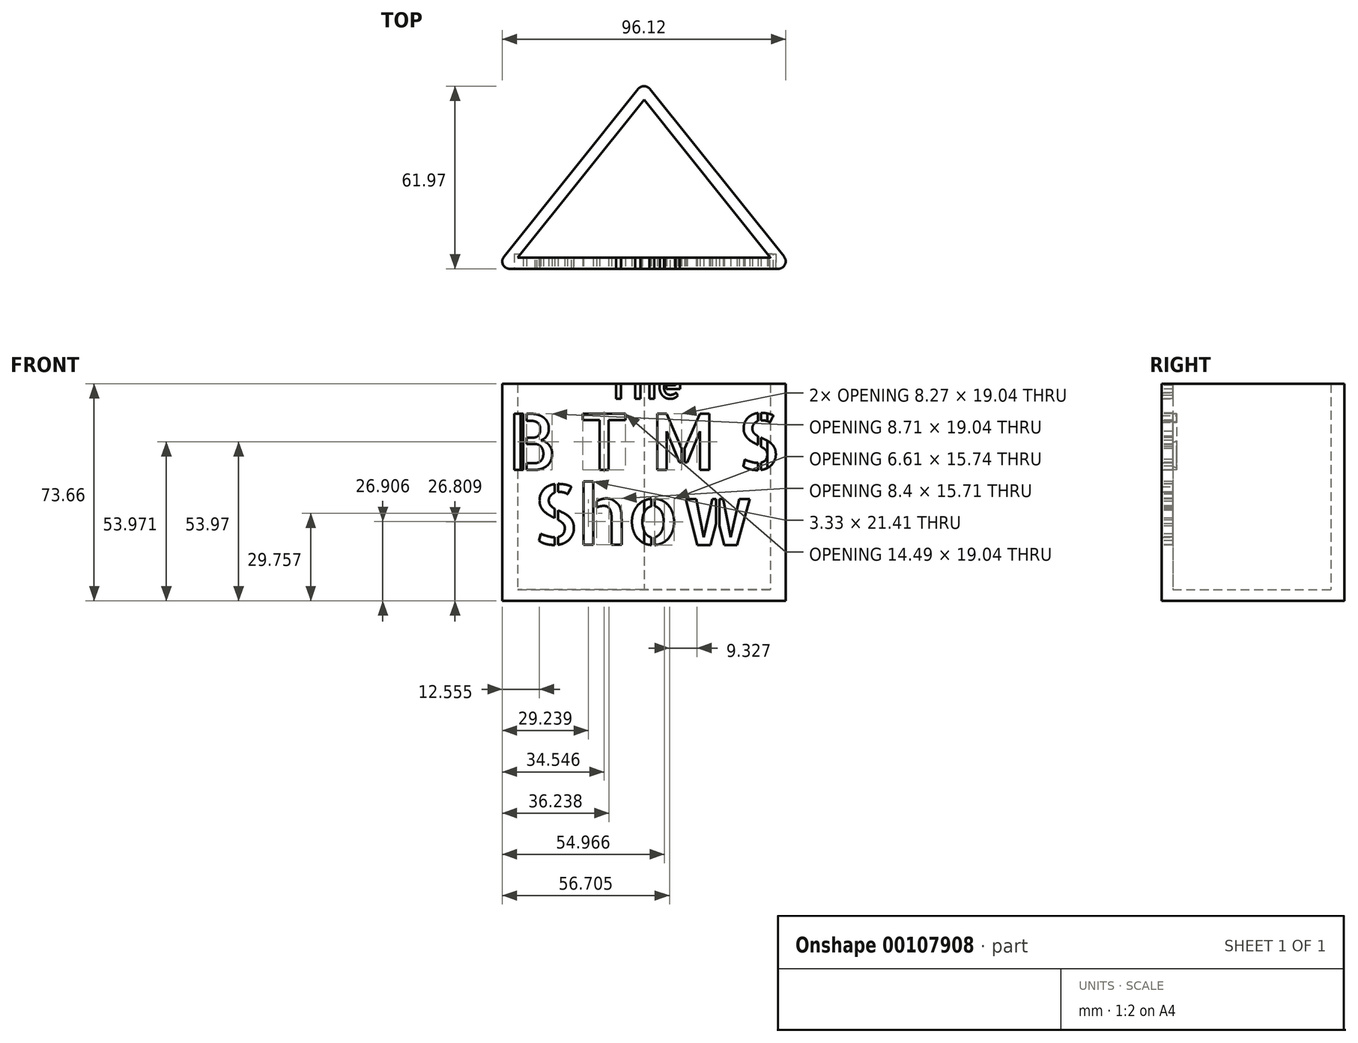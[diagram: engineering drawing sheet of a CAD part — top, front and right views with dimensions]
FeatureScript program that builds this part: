
annotation { "Feature Type Name" : "Feature", "Feature Type Description" : "" }
export const myFeature = defineFeature(function(context is Context, id is Id, definition is map)
    precondition{}
    {
        {
            var Q0;
            Q0=qCreatedBy(makeId("Top.planeOp"),FACE);
            var sketch = newSketch(context, id + "F0", { "sketchPlane" : qUnion([Q0])});
            skLineSegment(sketch, "E0", {"start": v(0, 0) * mm, "end": v(50.8, -63.5) * mm});
            skLineSegment(sketch, "E1", {"start": v(50.8, -63.5) * mm, "end": v(-50.8, -63.5) * mm});
            skLineSegment(sketch, "E2", {"start": v(-50.8, -63.5) * mm, "end": v(0, 0) * mm});
            skLineSegment(sketch, "E3", {"start": v(0, 0) * mm, "end": v(0, -63.5) * mm, "construction": true});
            skSolve(sketch);
        }
        {
            var Q0;
            Q0=makeQuery(id+"F0.imprint","IMPRINT",FACE,{"disambiguationData":[TD([[makeQuery(id+"F0.imprint","IMPRINT",EDGE,{"derivedFrom":sQuery(id+"F0.wireOp",EDGE,"E0")}),-1.0]])]});
            extrude(context, id + "F1", {"entities" : qUnion([Q0]), "depth" : 3.8 * mm});
        }
        {
            var Q0;
            Q0=makeQuery(id+"F1.opExtrude","CAP_FACE",FACE,{"disambiguationData":[OSD([sQuery(id+"F0.wireOp",EDGE,"E0"),sQuery(id+"F0.wireOp",EDGE,"E1"),sQuery(id+"F0.wireOp",EDGE,"E2")])],"isStart":false});
            var sketch = newSketch(context, id + "F2", { "sketchPlane" : qUnion([Q0])});
            skLineSegment(sketch, "E4.0", {"start": v(42.87, -59.7) * mm, "end": v(0, -6.1) * mm});
            skLineSegment(sketch, "E4.1", {"start": v(-42.87, -59.7) * mm, "end": v(42.87, -59.69) * mm});
            skLineSegment(sketch, "E4.2", {"start": v(0, -6.1) * mm, "end": v(-42.87, -59.7) * mm});
            skSolve(sketch);
        }
        {
            var Q0;
            Q0=makeQuery(id+"F2.imprint","IMPRINT",FACE,{"disambiguationData":[TD([[makeQuery(id+"F2.imprint","IMPRINT",EDGE,{"derivedFrom":sQuery(id+"F2.wireOp",EDGE,"E4.0")}),-1.0]])]});
            extrude(context, id + "F3", {"entities" : qUnion([Q0]), "operationType" : NewBodyOperationType.ADD, "depth" : 69.85 * mm});
        }
        {
            var Q0;
            {var subQ0=sQuery(id+"F0.wireOp",EDGE,"E1");Q0=makeQuery(id+"F3.boolean.opBoolean","MERGE",FACE,{"derivedFrom":[makeQuery(id+"F1.opExtrude","SWEPT_FACE",FACE,{"disambiguationData":[OSD([subQ0])]}),makeQuery(id+"F3.opExtrude","SWEPT_FACE",FACE,{"disambiguationData":[OSD([subQ0])]})]});}
            var sketch = newSketch(context, id + "F4", { "sketchPlane" : qUnion([Q0])});
            skText(sketch, "E5", { "text": "The", "fontName": "AllertaStencil-Regular.ttf"});
            skText(sketch, "E6", { "text": "B T M S", "fontName": "AllertaStencil-Regular.ttf"});
            skText(sketch, "E7", { "text": "Show", "fontName": "AllertaStencil-Regular.ttf"});
            skLineSegment(sketch, "E8", {"start": v(0, 73.66) * mm, "end": v(0, 0) * mm, "construction": true});
            const initialGuessF4  = {"E5": [-0.01326, 0.06858, 1, 0, 0.01016], "E6": [-0.0465, 0.04445, 1, 0, 0.01905], "E7": [-0.0378, 0.01905, 1, 0, 0.02032]};
            skSetInitialGuess(sketch, initialGuessF4);
            skSolve(sketch);
        }
        {
            var Q0;
            Q0 = qSketchRegion(id + "F4", true);
            extrude(context, id + "F5", {"entities" : qUnion([Q0]), "operationType" : NewBodyOperationType.REMOVE, "oppositeDirection" : true, "depth" : 5.08 * mm});
        }
        {
            var Q0;
            {var subQ0=sQuery(id+"F0.wireOp",EDGE,"E2");var subQ1=sQuery(id+"F0.wireOp",EDGE,"E0");Q0=makeQuery(id+"F3.boolean.opBoolean","MERGE",EDGE,{"derivedFrom":[makeQuery(id+"F1.opExtrude","SWEPT_EDGE",EDGE,{"disambiguationData":[OSD([subQ1,subQ0])]}),makeQuery(id+"F3.opExtrude","SWEPT_EDGE",EDGE,{"disambiguationData":[OSD([subQ1,subQ0])]})]});}
            var Q1;
            {var subQ0=sQuery(id+"F0.wireOp",EDGE,"E1");var subQ1=sQuery(id+"F0.wireOp",EDGE,"E0");Q1=makeQuery(id+"F3.boolean.opBoolean","MERGE",EDGE,{"derivedFrom":[makeQuery(id+"F1.opExtrude","SWEPT_EDGE",EDGE,{"disambiguationData":[OSD([subQ1,subQ0])]}),makeQuery(id+"F3.opExtrude","SWEPT_EDGE",EDGE,{"disambiguationData":[OSD([subQ1,subQ0])]})]});}
            var Q2;
            {var subQ0=sQuery(id+"F0.wireOp",EDGE,"E2");var subQ1=sQuery(id+"F0.wireOp",EDGE,"E1");Q2=makeQuery(id+"F3.boolean.opBoolean","MERGE",EDGE,{"derivedFrom":[makeQuery(id+"F1.opExtrude","SWEPT_EDGE",EDGE,{"disambiguationData":[OSD([subQ1,subQ0])]}),makeQuery(id+"F3.opExtrude","SWEPT_EDGE",EDGE,{"disambiguationData":[OSD([subQ1,subQ0])]})]});}
            fillet(context, id + "F6", {"entities" : qUnion([Q0, Q1, Q2]), "radius" : 2.54 * mm, "tangentPropagation" : true, "allowEdgeOverflow" : false});
        }
    });
